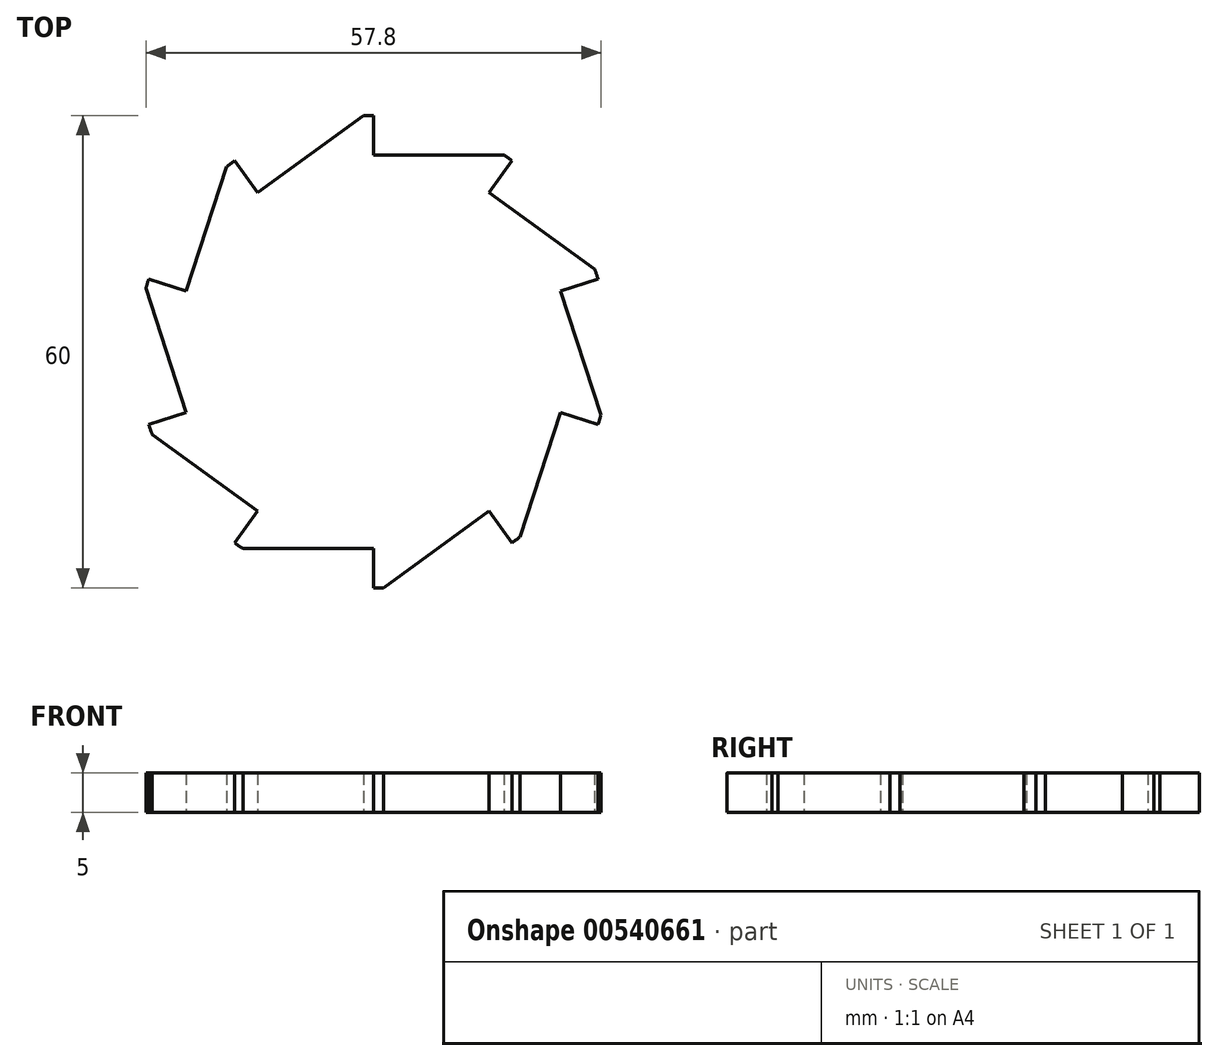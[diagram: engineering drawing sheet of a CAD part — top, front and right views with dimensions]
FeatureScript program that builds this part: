
annotation { "Feature Type Name" : "Feature", "Feature Type Description" : "" }
export const myFeature = defineFeature(function(context is Context, id is Id, definition is map)
    precondition{}
    {
        {
            var Q0;
            Q0=qCreatedBy(makeId("Top.planeOp"),FACE);
            var sketch = newSketch(context, id + "F0", { "sketchPlane" : qUnion([Q0])});
            skCircle(sketch, "E0", {"center": v(0, 0) * mm, "radius": 30 * mm});
            skLineSegment(sketch, "E1", {"start": v(0, 30) * mm, "end": v(0, 25) * mm});
            skLineSegment(sketch, "E2", {"start": v(0, 25) * mm, "end": v(16.58, 25) * mm});
            skLineSegment(sketch, "E3.1.0", {"start": v(-17.63, 24.27) * mm, "end": v(-14.7, 20.23) * mm});
            skLineSegment(sketch, "E3.1.1", {"start": v(-14.7, 20.23) * mm, "end": v(-1.28, 29.97) * mm});
            skLineSegment(sketch, "E3.2.0", {"start": v(-28.53, 9.27) * mm, "end": v(-23.78, 7.73) * mm});
            skLineSegment(sketch, "E3.2.1", {"start": v(-23.78, 7.73) * mm, "end": v(-18.65, 23.5) * mm});
            skLineSegment(sketch, "E4.2.3.0", {"start": v(-28.53, -9.27) * mm, "end": v(-23.78, -7.73) * mm});
            skLineSegment(sketch, "E4.3.3.0", {"start": v(-23.78, -7.73) * mm, "end": v(-28.9, 8.05) * mm});
            skLineSegment(sketch, "E4.2.4.0", {"start": v(-17.63, -24.27) * mm, "end": v(-14.7, -20.23) * mm});
            skLineSegment(sketch, "E4.3.4.0", {"start": v(-14.7, -20.23) * mm, "end": v(-28.11, -10.48) * mm});
            skLineSegment(sketch, "E4.2.5.0", {"start": v(0, -30) * mm, "end": v(0, -25) * mm});
            skLineSegment(sketch, "E4.3.5.0", {"start": v(0, -25) * mm, "end": v(-16.58, -25) * mm});
            skLineSegment(sketch, "E4.2.6.0", {"start": v(17.63, -24.27) * mm, "end": v(14.7, -20.23) * mm});
            skLineSegment(sketch, "E4.3.6.0", {"start": v(14.7, -20.23) * mm, "end": v(1.28, -29.97) * mm});
            skLineSegment(sketch, "E4.2.7.0", {"start": v(28.53, -9.27) * mm, "end": v(23.78, -7.73) * mm});
            skLineSegment(sketch, "E4.3.7.0", {"start": v(23.78, -7.73) * mm, "end": v(18.65, -23.5) * mm});
            skLineSegment(sketch, "E4.2.8.0", {"start": v(28.53, 9.27) * mm, "end": v(23.78, 7.73) * mm});
            skLineSegment(sketch, "E4.3.8.0", {"start": v(23.78, 7.73) * mm, "end": v(28.9, -8.05) * mm});
            skLineSegment(sketch, "E4.2.9.0", {"start": v(17.63, 24.27) * mm, "end": v(14.7, 20.23) * mm});
            skLineSegment(sketch, "E4.3.9.0", {"start": v(14.7, 20.23) * mm, "end": v(28.11, 10.48) * mm});
            skSolve(sketch);
        }
        {
            var Q0;
            {var subQ6=sQuery(id+"F0.wireOp",EDGE,"E1");Q0=makeQuery(id+"F0.imprint","IMPRINT",FACE,{"disambiguationData":[TD([[makeQuery(id+"F0.imprint","IMPRINT",EDGE,{"derivedFrom":subQ6}),-1.0]])]});}
            extrude(context, id + "F1", {"entities" : qUnion([Q0]), "depth" : 5 * mm, "offsetDistance" : 25 * mm});
        }
    });
